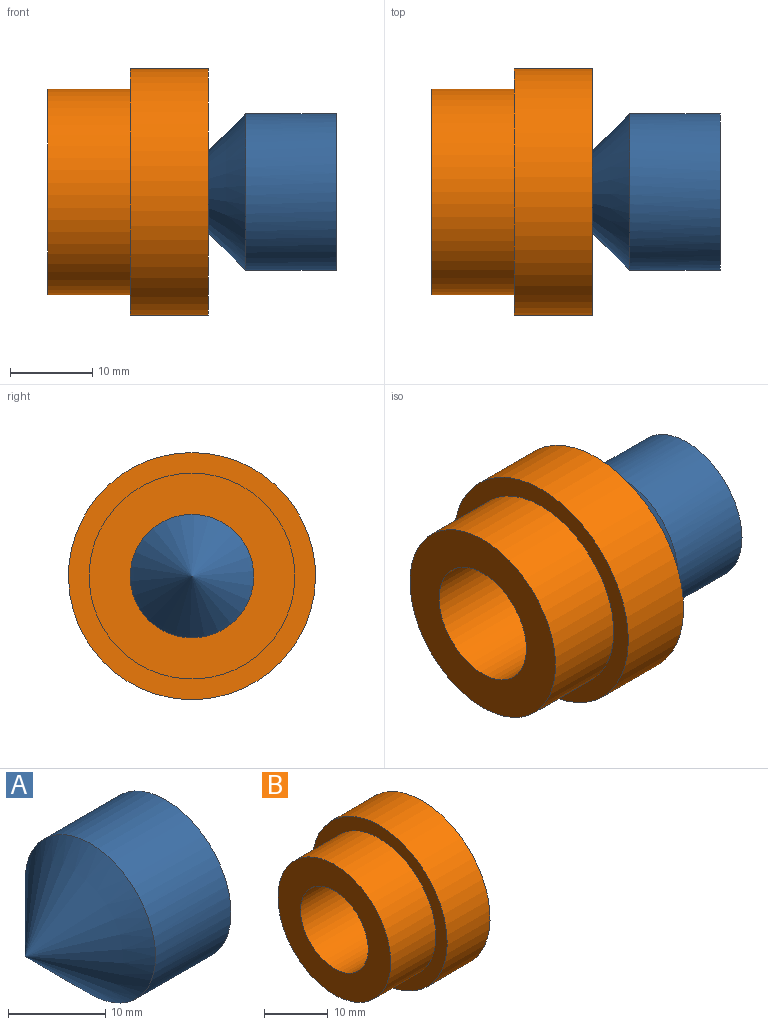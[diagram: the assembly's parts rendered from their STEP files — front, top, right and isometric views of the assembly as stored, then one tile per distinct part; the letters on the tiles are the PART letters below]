
ASSEMBLY  parts=2 mates=1
PART A: 3 faces, bbox 20.5x19x19 mm
  f0: plane 19x19mm, normal (1,0,0), area 283.5mm2, adj f1
  f1: cylinder r=9.5mm len=19mm, axis (-1,0,0), area 656.6mm2, adj f0,f2
  f2: cone r=0mm half-angle=45deg, axis (1,0,0), area 401mm2, adj f1
PART B: 6 faces, bbox 19.5x30x30 mm
  f0: cone r=15mm half-angle=45deg, axis (1,0,0), area 749.7mm2, adj f1,f5
  f1: cylinder r=15mm len=30mm, axis (-1,0,0), area 895.4mm2, adj f0,f2
  f2: plane 30x30mm, normal (-1,0,0), area 216mm2, adj f1,f3
  f3: cylinder r=12.5mm len=25mm, axis (-1,0,0), area 785.4mm2, adj f2,f4
  f4: plane 25x25mm, normal (-1,0,0), area 314.2mm2, adj f3,f5
  f5: cylinder r=7.5mm len=15mm, axis (-1,0,0), area 565.5mm2, adj f0,f4
PLACE A rot(axis=(-1,0,0),163.9deg) t=(14.11,8.96,-7.81)mm
PLACE B t=(-9.92,8.96,-7.81)mm fixed
MATE cylindrical B.f0 <-> A.f1  axis (-1,0,0) through (-3.92,8.96,-7.81)mm
